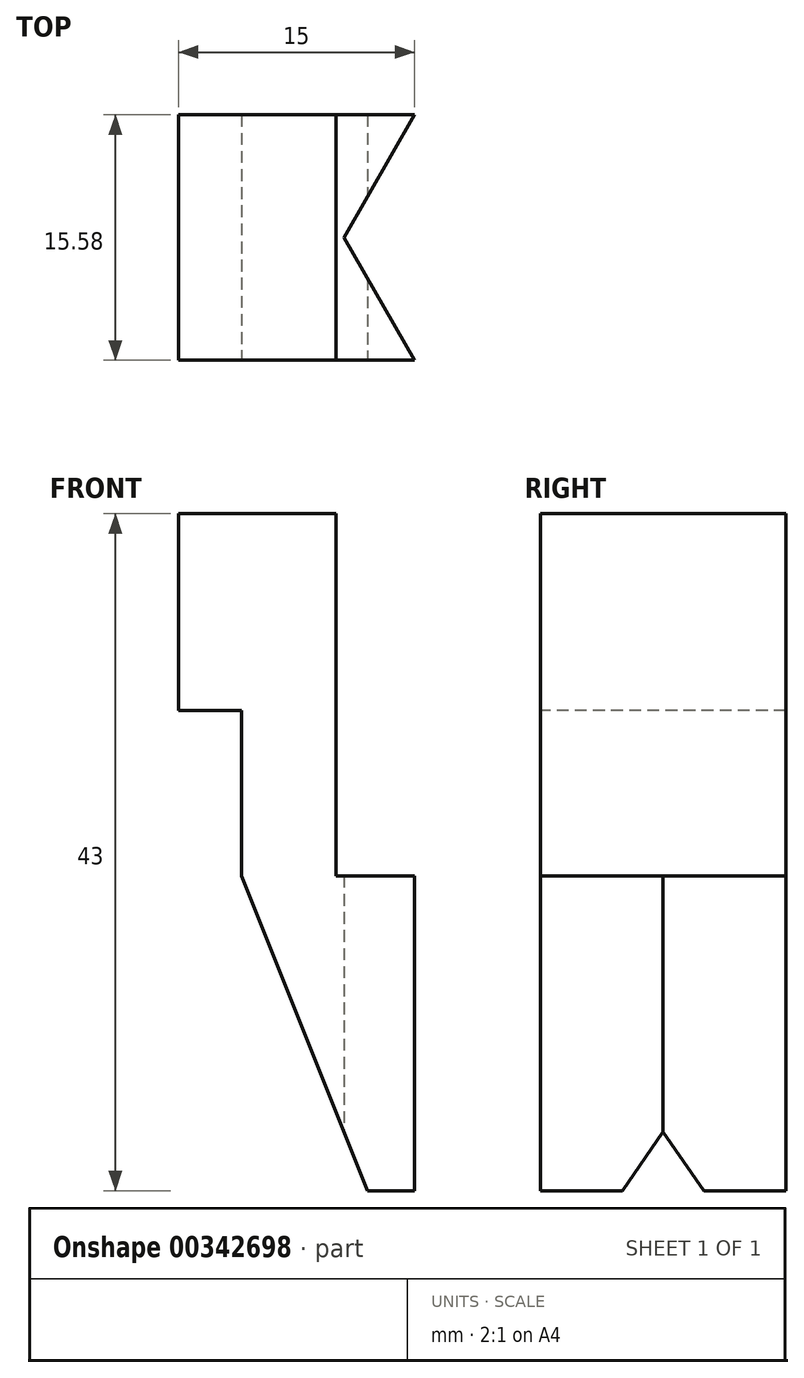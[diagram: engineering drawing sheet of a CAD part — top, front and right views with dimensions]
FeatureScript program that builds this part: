
annotation { "Feature Type Name" : "Feature", "Feature Type Description" : "" }
export const myFeature = defineFeature(function(context is Context, id is Id, definition is map)
    precondition{}
    {
        {
            var Q0;
            Q0=qCreatedBy(makeId("Top.planeOp"),FACE);
            var sketch = newSketch(context, id + "F0", { "sketchPlane" : qUnion([Q0])});
            skCircle(sketch, "E0", {"center": v(-11.5, 0) * mm, "radius": 9.5 * mm});
            skCircle(sketch, "E1", {"center": v(-14.4, 0) * mm, "radius": 7 * mm});
            skLineSegment(sketch, "E2.top", {"start": v(5.62, -8) * mm, "end": v(10.62, -8) * mm});
            skLineSegment(sketch, "E2.left", {"start": v(5.62, 0) * mm, "end": v(5.62, -8) * mm});
            skLineSegment(sketch, "E2.right", {"start": v(10.62, 0) * mm, "end": v(10.62, -8) * mm});
            skLineSegment(sketch, "E3", {"start": v(6.29, 0) * mm, "end": v(5.62, -2.48) * mm});
            skLineSegment(sketch, "E4.MirrorCS", {"start": v(6.29, 0) * mm, "end": v(5.62, 2.48) * mm});
            skLineSegment(sketch, "E5.MirrorCS", {"start": v(5.62, 0) * mm, "end": v(5.62, 8) * mm});
            skLineSegment(sketch, "E6", {"start": v(-10.48, 0) * mm, "end": v(-22.48, 0) * mm, "construction": true});
            skLineSegment(sketch, "E7", {"start": v(-22.48, 0) * mm, "end": v(-17.98, -7.8) * mm});
            skLineSegment(sketch, "E8.MirrorCS", {"start": v(5.62, 8) * mm, "end": v(10.62, 8) * mm});
            skLineSegment(sketch, "E9.MirrorCS", {"start": v(10.62, 0) * mm, "end": v(10.62, 8) * mm});
            skLineSegment(sketch, "E10", {"start": v(-17.98, -7.8) * mm, "end": v(-32.98, -7.8) * mm});
            skLineSegment(sketch, "E11.MirrorCS", {"start": v(-22.48, 0) * mm, "end": v(-17.98, 7.8) * mm});
            skLineSegment(sketch, "E12.MirrorCS", {"start": v(-17.98, 7.8) * mm, "end": v(-32.98, 7.8) * mm});
            skLineSegment(sketch, "E13", {"start": v(-32.98, 7.8) * mm, "end": v(-32.98, -7.8) * mm});
            skLineSegment(sketch, "E14", {"start": v(-22.98, 7.8) * mm, "end": v(-22.98, -7.8) * mm});
            skSolve(sketch);
        }
        {
            var Q0;
            {var subQ5=sQuery(id+"F0.wireOp",EDGE,"E14");Q0=makeQuery(id+"F0.imprint","IMPRINT",FACE,{"disambiguationData":[TD([[makeQuery(id+"F0.imprint","IMPRINT",EDGE,{"derivedFrom":subQ5}),1.0]])]});}
            var Q1;
            {var subQ0=sQuery(id+"F0.wireOp",EDGE,"E13");Q1=makeQuery(id+"F0.imprint","IMPRINT",FACE,{"disambiguationData":[TD([[makeQuery(id+"F0.imprint","IMPRINT",EDGE,{"derivedFrom":subQ0}),1.0]])]});}
            extrude(context, id + "F1", {"entities" : qUnion([Q0, Q1]), "depth" : 20 * mm});
        }
        {
            var Q0;
            Q0=makeQuery(id+"F1.opExtrude","CAP_FACE",FACE,{"disambiguationData":[OSD([sQuery(id+"F0.wireOp",EDGE,"E7"),sQuery(id+"F0.wireOp",EDGE,"E10"),sQuery(id+"F0.wireOp",EDGE,"E11.MirrorCS"),sQuery(id+"F0.wireOp",EDGE,"E12.MirrorCS"),sQuery(id+"F0.wireOp",EDGE,"E13")])],"isStart":false});
            var sketch = newSketch(context, id + "F2", { "sketchPlane" : qUnion([Q0])});
            skLineSegment(sketch, "E15.0", {"start": v(-32.98, 7.8) * mm, "end": v(-32.98, -7.8) * mm});
            skLineSegment(sketch, "E15.1", {"start": v(-22.98, 7.8) * mm, "end": v(-22.98, -7.8) * mm});
            skLineSegment(sketch, "E16", {"start": v(-32.98, 7.8) * mm, "end": v(-22.98, 7.8) * mm});
            skLineSegment(sketch, "E17", {"start": v(-32.98, -7.8) * mm, "end": v(-22.98, -7.8) * mm});
            skSolve(sketch);
        }
        {
            var Q0;
            Q0=makeQuery(id+"F2.imprint","IMPRINT",FACE,{"disambiguationData":[TD([[makeQuery(id+"F2.imprint","IMPRINT",EDGE,{"derivedFrom":sQuery(id+"F2.wireOp",EDGE,"E15.0")}),1.0]])]});
            extrude(context, id + "F3", {"entities" : qUnion([Q0]), "operationType" : NewBodyOperationType.ADD, "depth" : 23 * mm});
        }
        {
            var Q0;
            Q0=makeQuery(id+"F3.boolean.opBoolean","MERGE",FACE,{"derivedFrom":[makeQuery(id+"F1.opExtrude","SWEPT_FACE",FACE,{"disambiguationData":[OSD([sQuery(id+"F0.wireOp",EDGE,"E10")])]}),makeQuery(id+"F3.opExtrude","SWEPT_FACE",FACE,{"disambiguationData":[OSD([sQuery(id+"FiaceHbDWvn0p0G_1.wireOp",EDGE,"O1DIgB5I-w2EE-7dS8-mdiZ-9omDXuDUg0lk")])]})]});
            var sketch = newSketch(context, id + "F4", { "sketchPlane" : qUnion([Q0])});
            skPoint(sketch, "E18.1", {"position": v(-17.98, 10) * mm});
            skLineSegment(sketch, "E19.0", {"start": v(-17.98, 20) * mm, "end": v(-17.98, 0) * mm});
            skLineSegment(sketch, "E20", {"start": v(-32.98, 30.5) * mm, "end": v(-22.98, 30.5) * mm});
            skLineSegment(sketch, "E21", {"start": v(-28.98, 30.5) * mm, "end": v(-28.98, 0) * mm});
            skLineSegment(sketch, "E22.0", {"start": v(-32.98, 43) * mm, "end": v(-32.98, 0) * mm});
            skLineSegment(sketch, "E23.0", {"start": v(-17.98, 0) * mm, "end": v(-32.98, 0) * mm});
            skLineSegment(sketch, "E24", {"start": v(-17.98, 0) * mm, "end": v(-20.98, 0) * mm, "construction": true});
            skLineSegment(sketch, "E25", {"start": v(-20.98, 0) * mm, "end": v(-28.98, 20) * mm});
            skSolve(sketch);
        }
        {
            var Q0;
            {var subQ1=sQuery(id+"F4.wireOp",EDGE,"E22.0");var subQ3=sQuery(id+"F4.wireOp",EDGE,"E20");var subQ4=makeQuery(id+"F4.imprint","INTERSECT",VERTEX,{"derivedFrom":[subQ3,subQ1]});Q0=makeQuery(id+"F4.imprint","IMPRINT",FACE,{"disambiguationData":[TD([[makeQuery(id+"F4.imprint","IMPRINT",EDGE,{"disambiguationData":[TD([[subQ4,-1.0]])],"derivedFrom":subQ3}),-1.0]])]});}
            extrude(context, id + "F5", {"entities" : qUnion([Q0]), "operationType" : NewBodyOperationType.REMOVE, "endBound" : BoundingType.THROUGH_ALL, "oppositeDirection" : true, "depth" : 25 * mm});
        }
        {
            var Q0;
            {var subQ3=sQuery(id+"F4.wireOp",EDGE,"E25");Q0=makeQuery(id+"F4.imprint","IMPRINT",FACE,{"disambiguationData":[TD([[makeQuery(id+"F4.imprint","IMPRINT",EDGE,{"derivedFrom":subQ3}),1.0]])]});}
            extrude(context, id + "F6", {"entities" : qUnion([Q0]), "operationType" : NewBodyOperationType.REMOVE, "endBound" : BoundingType.THROUGH_ALL, "oppositeDirection" : true, "depth" : 25 * mm});
        }
    });
